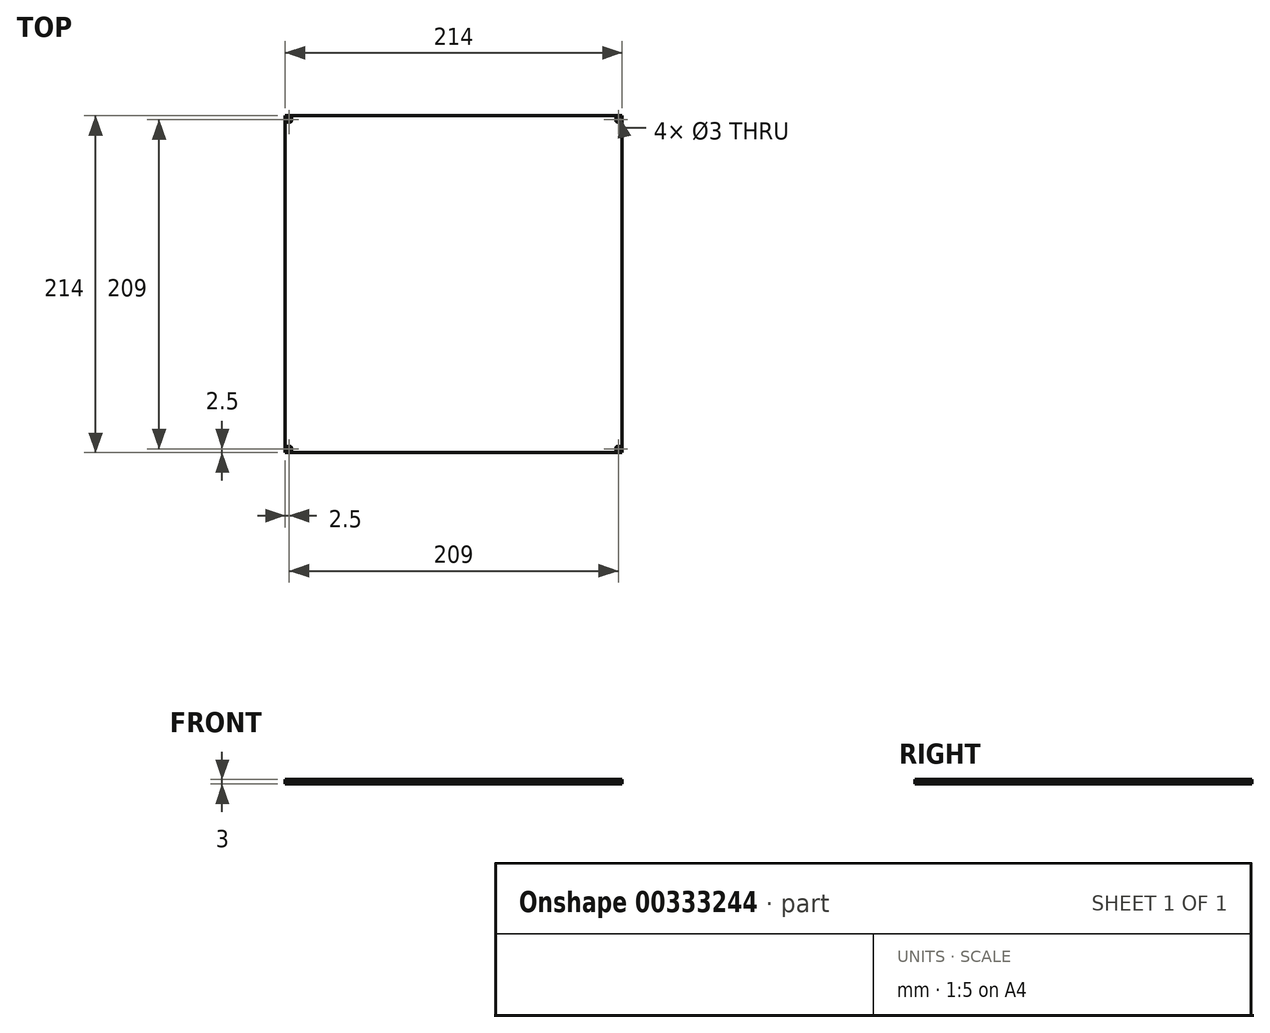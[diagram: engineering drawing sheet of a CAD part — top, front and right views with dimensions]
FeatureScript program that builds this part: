
annotation { "Feature Type Name" : "Feature", "Feature Type Description" : "" }
export const myFeature = defineFeature(function(context is Context, id is Id, definition is map)
    precondition{}
    {
        {
            var Q0;
            Q0=qCreatedBy(makeId("Top.planeOp"),FACE);
            var sketch = newSketch(context, id + "F0", { "sketchPlane" : qUnion([Q0])});
            skLineSegment(sketch, "E0.bottom", {"start": v(107, 107) * mm, "end": v(-107, 107) * mm});
            skLineSegment(sketch, "E0.top", {"start": v(107, -107) * mm, "end": v(-107, -107) * mm});
            skLineSegment(sketch, "E0.left", {"start": v(107, 107) * mm, "end": v(107, -107) * mm});
            skLineSegment(sketch, "E0.right", {"start": v(-107, 107) * mm, "end": v(-107, -107) * mm});
            skPoint(sketch, "E0.middle", {"position": v(0, 0) * mm});
            skLineSegment(sketch, "E1.bottom", {"start": v(104.5, 104.5) * mm, "end": v(-104.5, 104.5) * mm, "construction": true});
            skLineSegment(sketch, "E1.top", {"start": v(104.5, -104.5) * mm, "end": v(-104.5, -104.5) * mm, "construction": true});
            skLineSegment(sketch, "E1.left", {"start": v(104.5, 104.5) * mm, "end": v(104.5, -104.5) * mm, "construction": true});
            skLineSegment(sketch, "E1.right", {"start": v(-104.5, 104.5) * mm, "end": v(-104.5, -104.5) * mm, "construction": true});
            skLineSegment(sketch, "E2", {"start": v(-102, 107) * mm, "end": v(-107, 102) * mm});
            skLineSegment(sketch, "E3", {"start": v(107, 102) * mm, "end": v(102, 107) * mm});
            skLineSegment(sketch, "E4", {"start": v(-102, -107) * mm, "end": v(-107, -102) * mm});
            skLineSegment(sketch, "E5", {"start": v(107, -102) * mm, "end": v(102, -107) * mm});
            skSolve(sketch);
        }
        {
            var Q0;
            {var subQ0=sQuery(id+"F0.wireOp",EDGE,"E2");Q0=makeQuery(id+"F0.imprint","IMPRINT",FACE,{"disambiguationData":[TD([[makeQuery(id+"F0.imprint","IMPRINT",EDGE,{"derivedFrom":subQ0}),1.0]])]});}
            extrude(context, id + "F1", {"entities" : qUnion([Q0]), "depth" : 1 * mm});
        }
        {
            var Q0;
            {var subQ3=sQuery(id+"F0.wireOp",EDGE,"E4");Q0=makeQuery(id+"F0.imprint","IMPRINT",FACE,{"disambiguationData":[TD([[makeQuery(id+"F0.imprint","IMPRINT",EDGE,{"derivedFrom":subQ3}),1.0]])]});}
            var Q1;
            {var subQ0=sQuery(id+"F0.wireOp",EDGE,"E2");Q1=makeQuery(id+"F0.imprint","IMPRINT",FACE,{"disambiguationData":[TD([[makeQuery(id+"F0.imprint","IMPRINT",EDGE,{"derivedFrom":subQ0}),1.0]])]});}
            var Q2;
            {var subQ3=sQuery(id+"F0.wireOp",EDGE,"E5");Q2=makeQuery(id+"F0.imprint","IMPRINT",FACE,{"disambiguationData":[TD([[makeQuery(id+"F0.imprint","IMPRINT",EDGE,{"derivedFrom":subQ3}),1.0]])]});}
            var Q3;
            {var subQ3=sQuery(id+"F0.wireOp",EDGE,"E3");Q3=makeQuery(id+"F0.imprint","IMPRINT",FACE,{"disambiguationData":[TD([[makeQuery(id+"F0.imprint","IMPRINT",EDGE,{"derivedFrom":subQ3}),-1.0]])]});}
            var Q4;
            {var subQ3=sQuery(id+"F0.wireOp",EDGE,"E2");Q4=makeQuery(id+"F0.imprint","IMPRINT",FACE,{"disambiguationData":[TD([[makeQuery(id+"F0.imprint","IMPRINT",EDGE,{"derivedFrom":subQ3}),-1.0]])]});}
            extrude(context, id + "F2", {"entities" : qUnion([Q0, Q1, Q2, Q3, Q4]), "oppositeDirection" : true, "depth" : 1 * mm});
        }
        {
            var Q0;
            Q0=sQuery(id+"F0.wireOp",VERTEX,"E1.bottom.end");
            var Q1;
            Q1=sQuery(id+"F0.wireOp",VERTEX,"E1.top.end");
            var Q2;
            Q2=sQuery(id+"F0.wireOp",VERTEX,"E1.top.start");
            var Q3;
            Q3=sQuery(id+"F0.wireOp",VERTEX,"E1.left.start");
            var Q4;
            Q4=makeQuery(id+"F2.opExtrude","SWEPT_BODY",BODY,{"disambiguationData":[OSD([sQuery(id+"F0.wireOp",EDGE,"E0.bottom"),sQuery(id+"F0.wireOp",EDGE,"E0.top"),sQuery(id+"F0.wireOp",EDGE,"E0.left"),sQuery(id+"F0.wireOp",EDGE,"E0.right")])]});
            var Q5;
            Q5=makeQuery(id+"F1.opExtrude","SWEPT_BODY",BODY,{"disambiguationData":[OSD([sQuery(id+"F0.wireOp",EDGE,"E0.bottom"),sQuery(id+"F0.wireOp",EDGE,"E0.top"),sQuery(id+"F0.wireOp",EDGE,"E0.left"),sQuery(id+"F0.wireOp",EDGE,"E0.right"),sQuery(id+"F0.wireOp",EDGE,"E2"),sQuery(id+"F0.wireOp",EDGE,"E3"),sQuery(id+"F0.wireOp",EDGE,"E4"),sQuery(id+"F0.wireOp",EDGE,"E5")])]});
            hole(context, id + "F3", {"style" : HoleStyle.SIMPLE, "endStyle" : HoleEndStyle.THROUGH, "holeDiameter" : 3 * mm, "tappedDepth" : 12 * mm, "tapClearance" : 3, "locations" : qUnion([Q0, Q1, Q2, Q3]), "scope" : qUnion([Q4, Q5])});
        }
        {
            var Q0;
            {var subQ0=sQuery(id+"F0.wireOp",EDGE,"E2");Q0=makeQuery(id+"F0.imprint","IMPRINT",FACE,{"disambiguationData":[TD([[makeQuery(id+"F0.imprint","IMPRINT",EDGE,{"derivedFrom":subQ0}),1.0]])]});}
            extrude(context, id + "F4", {"entities" : qUnion([Q0]), "oppositeDirection" : true, "depth" : 2 * mm, "hasSecondDirection" : true, "secondDirectionOppositeDirection" : true, "secondDirectionDepth" : 1 * mm});
        }
        {
            var Q0;
            {var subQ0=sQuery(id+"F0.wireOp",EDGE,"E2");Q0=makeQuery(id+"F0.imprint","IMPRINT",FACE,{"disambiguationData":[TD([[makeQuery(id+"F0.imprint","IMPRINT",EDGE,{"derivedFrom":subQ0}),1.0]])]});}
            var sketch = newSketch(context, id + "F5", { "sketchPlane" : qUnion([Q0])});
            skPoint(sketch, "E6.0", {"position": v(-104.5, 104.5) * mm});
            skPoint(sketch, "E7.0", {"position": v(-104.5, -104.5) * mm});
            skPoint(sketch, "E8.0", {"position": v(104.5, -104.5) * mm});
            skPoint(sketch, "E9.0", {"position": v(104.5, 104.5) * mm});
            skSolve(sketch);
        }
        {
            var Q0;
            Q0=sQuery(id+"F5.wireOp",VERTEX,"E7.0");
            var Q1;
            Q1=sQuery(id+"F5.wireOp",VERTEX,"E6.0");
            var Q2;
            Q2=sQuery(id+"F5.wireOp",VERTEX,"E9.0");
            var Q3;
            Q3=sQuery(id+"F5.wireOp",VERTEX,"E8.0");
            var Q4;
            Q4=makeQuery(id+"F1.opExtrude","SWEPT_BODY",BODY,{"disambiguationData":[OSD([sQuery(id+"F0.wireOp",EDGE,"E0.bottom"),sQuery(id+"F0.wireOp",EDGE,"E0.top"),sQuery(id+"F0.wireOp",EDGE,"E0.left"),sQuery(id+"F0.wireOp",EDGE,"E0.right"),sQuery(id+"F0.wireOp",EDGE,"E2"),sQuery(id+"F0.wireOp",EDGE,"E3"),sQuery(id+"F0.wireOp",EDGE,"E4"),sQuery(id+"F0.wireOp",EDGE,"E5")])]});
            hole(context, id + "F6", {"style" : HoleStyle.SIMPLE, "endStyle" : HoleEndStyle.THROUGH, "oppositeDirection" : true, "standardTappedOrClearance" : lookupTablePath({ "standard" : "ISO", "fit" : "Normal", "size" : "M3", "type" : "Clearance" }), "standardBlindInLast" : lookupTablePath({ "fit" : "Standard", "standard" : "ISO", "size" : "M3", "type" : "Clearance" }), "holeDiameter" : 3.3 * mm, "tappedDepth" : 12 * mm, "tapClearance" : 3, "locations" : qUnion([Q0, Q1, Q2, Q3]), "scope" : qUnion([Q4])});
        }
    });
